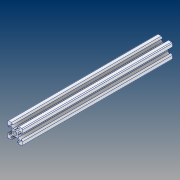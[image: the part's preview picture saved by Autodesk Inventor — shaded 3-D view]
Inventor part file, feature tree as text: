
AUTODESK INVENTOR PART (.ipt)
format: ipt  version: 2021 (Build 250183000, 183)  size: 166,912 bytes
history: native  units: mm
features: extrude x1, sketch x1
ambient origin geometry x8: Origin, YZ Plane, XZ Plane, XY Plane, X Axis, Y Axis, Z Axis, Center Point
bodies: Solid1 (feature_tree)
feature tree (2):
  extrude  "Extrusion1"  Depth=200.0mm TaperAngle=0.0deg
  sketch  "Sketch1"  dims[d1=40.0mm d2=360.0deg d3=200.0mm d4=0.0mm]
